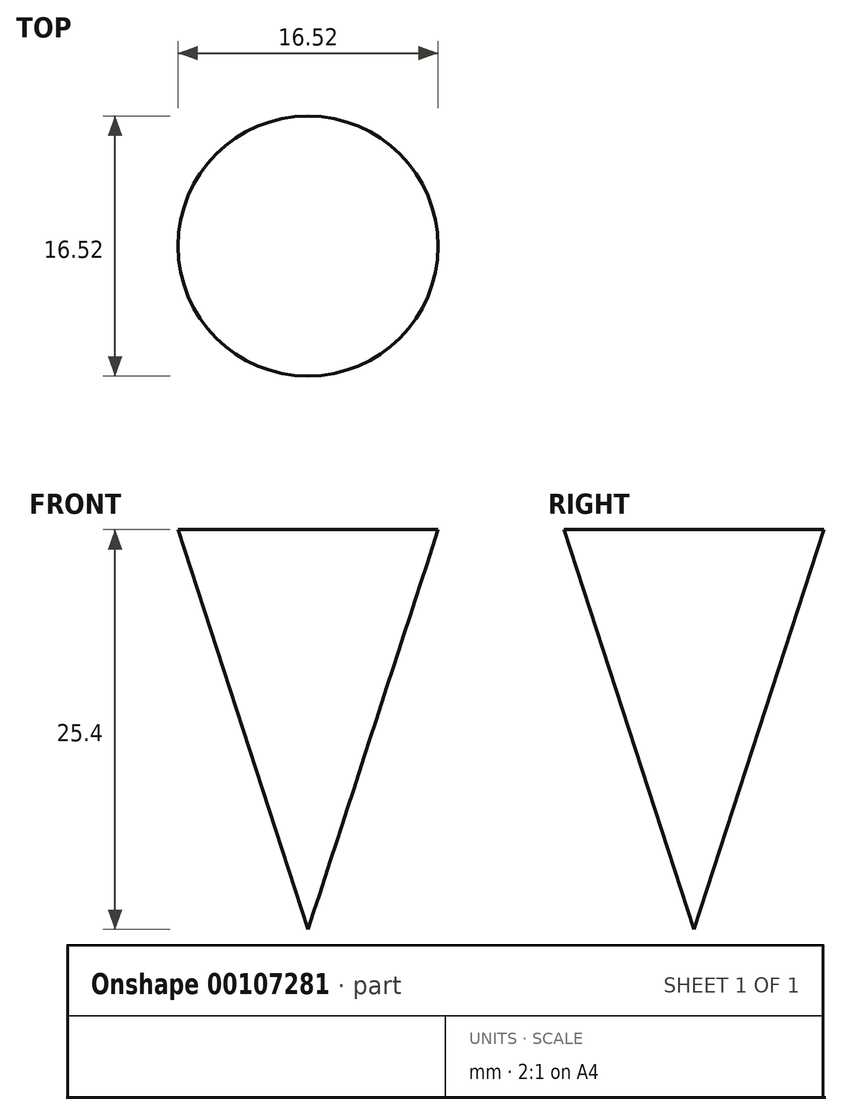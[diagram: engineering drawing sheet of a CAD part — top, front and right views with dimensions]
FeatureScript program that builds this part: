
annotation { "Feature Type Name" : "Feature", "Feature Type Description" : "" }
export const myFeature = defineFeature(function(context is Context, id is Id, definition is map)
    precondition{}
    {
        {
            var Q0;
            Q0=qCreatedBy(makeId("Front.planeOp"),FACE);
            var sketch = newSketch(context, id + "F0", { "sketchPlane" : qUnion([Q0])});
            skLineSegment(sketch, "E0", {"start": v(0, 0) * mm, "end": v(0, 25.4) * mm});
            skLineSegment(sketch, "E1", {"start": v(0, 25.4) * mm, "end": v(8.26, 25.4) * mm});
            skLineSegment(sketch, "E2", {"start": v(8.26, 25.4) * mm, "end": v(0, 0) * mm});
            skSolve(sketch);
        }
        {
            var Q0;
            Q0=makeQuery(id+"F0.imprint","IMPRINT",FACE,{"disambiguationData":[TD([[makeQuery(id+"F0.imprint","IMPRINT",EDGE,{"derivedFrom":sQuery(id+"F0.wireOp",EDGE,"E0")}),-1.0]])]});
            var Q1;
            Q1=sQuery(id+"F0.wireOp",EDGE,"E0");
            revolve(context, id + "F1", {"entities" : qUnion([Q0]), "axis" : qUnion([Q1]), "revolveType" : RevolveType.FULL});
        }
    });
